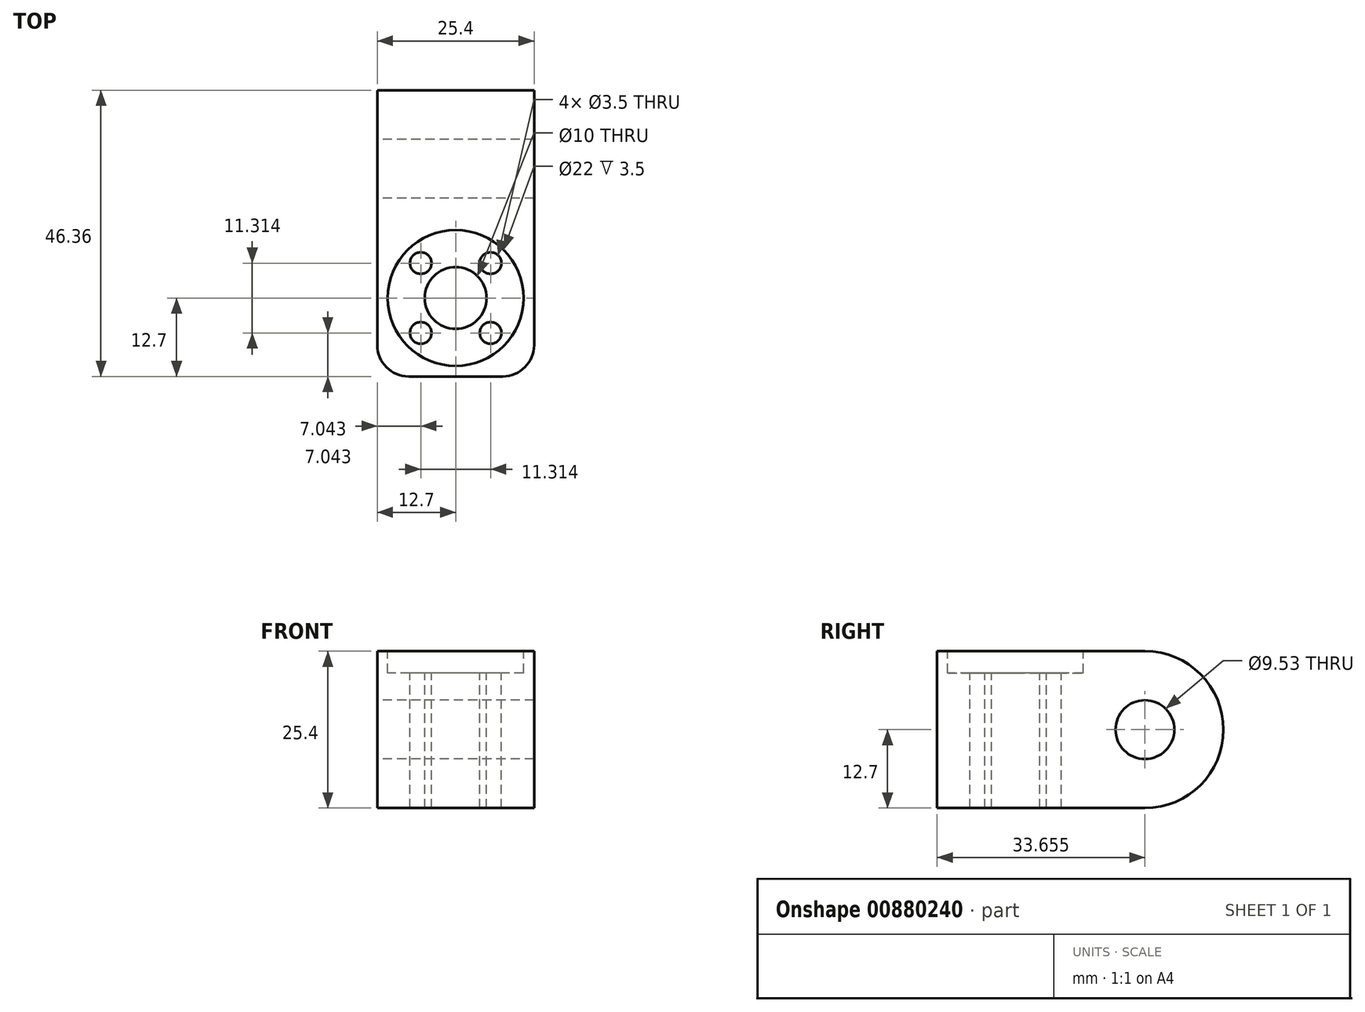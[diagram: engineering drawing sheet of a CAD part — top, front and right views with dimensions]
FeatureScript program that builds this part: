
annotation { "Feature Type Name" : "Feature", "Feature Type Description" : "" }
export const myFeature = defineFeature(function(context is Context, id is Id, definition is map)
    precondition{}
    {
        {
            var Q0;
            Q0=qCreatedBy(makeId("Top.planeOp"),FACE);
            var sketch = newSketch(context, id + "F0", { "sketchPlane" : qUnion([Q0])});
            skLineSegment(sketch, "E0.bottom", {"start": v(12.7, 12.7) * mm, "end": v(-12.7, 12.7) * mm});
            skLineSegment(sketch, "E0.top", {"start": v(12.7, -12.7) * mm, "end": v(-12.7, -12.7) * mm});
            skLineSegment(sketch, "E0.left", {"start": v(12.7, 12.7) * mm, "end": v(12.7, -12.7) * mm});
            skLineSegment(sketch, "E0.right", {"start": v(-12.7, 12.7) * mm, "end": v(-12.7, -12.7) * mm});
            skPoint(sketch, "E0.middle", {"position": v(0, 0) * mm});
            skSolve(sketch);
        }
        {
            var Q0;
            Q0=qSketchRegion(id+"F0",true);
            extrude(context, id + "F1", {"entities" : qUnion([Q0]), "depth" : 25.4 * mm});
        }
        {
            var Q0;
            Q0=qCreatedBy(makeId("Right.planeOp"),FACE);
            var sketch = newSketch(context, id + "F2", { "sketchPlane" : qUnion([Q0])});
            skCircle(sketch, "E1", {"center": v(20.96, 12.7) * mm, "radius": 4.76 * mm});
            skArc(sketch, "E2", {"start": v(20.96, 0) * mm, "mid": v(33.66, 12.7) * mm, "end": v(20.96, 25.4) * mm});
            skLineSegment(sketch, "E3", {"start": v(12.7, 25.4) * mm, "end": v(12.7, 0) * mm});
            skLineSegment(sketch, "E4", {"start": v(12.7, 0) * mm, "end": v(20.96, 0) * mm});
            skLineSegment(sketch, "E5", {"start": v(12.7, 25.4) * mm, "end": v(20.96, 25.4) * mm});
            skLineSegment(sketch, "E6", {"start": v(12.7, 12.7) * mm, "end": v(20.96, 12.7) * mm, "construction": true});
            skSolve(sketch);
        }
        {
            var Q0;
            Q0=qSketchRegion(id+"F2",true);
            var Q1;
            Q1=makeQuery(id+"F1.opExtrude","SWEPT_FACE",FACE,{"disambiguationData":[OSD([sQuery(id+"F0.wireOp",EDGE,"E0.left")])]});
            var Q2;
            Q2=makeQuery(id+"F1.opExtrude","SWEPT_FACE",FACE,{"disambiguationData":[OSD([sQuery(id+"F0.wireOp",EDGE,"E0.right")])]});
            extrude(context, id + "F3", {"entities" : qUnion([Q0]), "operationType" : NewBodyOperationType.ADD, "endBound" : BoundingType.UP_TO_SURFACE, "endBoundEntityFace" : qUnion([Q1]), "depth" : 11.43 * mm, "hasSecondDirection" : true, "secondDirectionBound" : BoundingType.UP_TO_SURFACE, "secondDirectionOppositeDirection" : true, "secondDirectionBoundEntityFace" : qUnion([Q2]), "secondDirectionDepth" : 6.35 * mm});
        }
        {
            var Q0;
            Q0=makeQuery(id+"FQh9y1oBI0PSwnX_1.boolean.opBoolean","MERGE",EDGE,{"derivedFrom":[makeQuery(id+"F1.opExtrude","SWEPT_EDGE",EDGE,{"disambiguationData":[OSD([sQuery(id+"F0.wireOp",EDGE,"E0.top"),sQuery(id+"F0.wireOp",EDGE,"E0.right")])]}),makeQuery(id+"FQh9y1oBI0PSwnX_1.opExtrude","SWEPT_EDGE",EDGE,{"disambiguationData":[OSD([sQuery(id+"FoaR56RkUjx8Qlo_1.wireOp",EDGE,"80af4be5-76a2-4d3a-8f25-b1f0519251b4.0"),sQuery(id+"FoaR56RkUjx8Qlo_1.wireOp",EDGE,"cc0fe09c-0044-47d0-847c-5cf717c9cb56.0")])]})]});
            var Q1;
            Q1=makeQuery(id+"FQh9y1oBI0PSwnX_1.boolean.opBoolean","MERGE",EDGE,{"derivedFrom":[makeQuery(id+"F1.opExtrude","SWEPT_EDGE",EDGE,{"disambiguationData":[OSD([sQuery(id+"F0.wireOp",EDGE,"E0.top"),sQuery(id+"F0.wireOp",EDGE,"E0.left")])]}),makeQuery(id+"FQh9y1oBI0PSwnX_1.opExtrude","SWEPT_EDGE",EDGE,{"disambiguationData":[OSD([sQuery(id+"FoaR56RkUjx8Qlo_1.wireOp",EDGE,"9dc4b1c0-afcf-448b-8161-34d6e761d681.0"),sQuery(id+"FoaR56RkUjx8Qlo_1.wireOp",EDGE,"80af4be5-76a2-4d3a-8f25-b1f0519251b4.0")])]})]});
            fillet(context, id + "F4", {"entities" : qUnion([Q0, Q1]), "radius" : 5.08 * mm, "tangentPropagation" : true, "allowEdgeOverflow" : false});
        }
        {
            var Q0;
            Q0=makeQuery(id+"F3.boolean.opBoolean","MERGE",FACE,{"derivedFrom":[makeQuery(id+"F1.opExtrude","CAP_FACE",FACE,{"disambiguationData":[OSD([sQuery(id+"F0.wireOp",EDGE,"E0.bottom"),sQuery(id+"F0.wireOp",EDGE,"E0.top"),sQuery(id+"F0.wireOp",EDGE,"E0.left"),sQuery(id+"F0.wireOp",EDGE,"E0.right")])],"isStart":false}),makeQuery(id+"F3.opExtrude","SWEPT_FACE",FACE,{"disambiguationData":[OSD([sQuery(id+"F2.wireOp",EDGE,"E5")])]})]});
            var sketch = newSketch(context, id + "F5", { "sketchPlane" : qUnion([Q0])});
            skCircle(sketch, "E7", {"center": v(0, 0) * mm, "radius": 5 * mm});
            skCircle(sketch, "E8", {"center": v(-5.66, 5.66) * mm, "radius": 1.75 * mm});
            skCircle(sketch, "E9", {"center": v(0, 0) * mm, "radius": 8 * mm, "construction": true});
            skCircle(sketch, "E10", {"center": v(5.66, 5.66) * mm, "radius": 1.75 * mm});
            skCircle(sketch, "E11", {"center": v(5.66, -5.66) * mm, "radius": 1.75 * mm});
            skCircle(sketch, "E12", {"center": v(-5.66, -5.66) * mm, "radius": 1.75 * mm});
            skLineSegment(sketch, "E13", {"start": v(5.66, 5.66) * mm, "end": v(-5.66, 5.66) * mm, "construction": true});
            skLineSegment(sketch, "E14", {"start": v(-5.66, -5.66) * mm, "end": v(-5.66, 5.66) * mm, "construction": true});
            skLineSegment(sketch, "E15", {"start": v(-5.66, -5.66) * mm, "end": v(5.66, -5.66) * mm});
            skSolve(sketch);
        }
        {
            var Q0;
            Q0=qSketchRegion(id+"F5",true);
            extrude(context, id + "F6", {"entities" : qUnion([Q0]), "operationType" : NewBodyOperationType.REMOVE, "endBound" : BoundingType.THROUGH_ALL, "oppositeDirection" : true, "depth" : 25.4 * mm});
        }
        {
            var Q0;
            Q0=makeQuery(id+"F3.boolean.opBoolean","MERGE",FACE,{"derivedFrom":[makeQuery(id+"F1.opExtrude","CAP_FACE",FACE,{"disambiguationData":[OSD([sQuery(id+"F0.wireOp",EDGE,"E0.bottom"),sQuery(id+"F0.wireOp",EDGE,"E0.top"),sQuery(id+"F0.wireOp",EDGE,"E0.left"),sQuery(id+"F0.wireOp",EDGE,"E0.right")])],"isStart":false}),makeQuery(id+"F3.opExtrude","SWEPT_FACE",FACE,{"disambiguationData":[OSD([sQuery(id+"F2.wireOp",EDGE,"E5")])]})]});
            var sketch = newSketch(context, id + "F7", { "sketchPlane" : qUnion([Q0])});
            skCircle(sketch, "E16", {"center": v(0, 0) * mm, "radius": 11 * mm});
            skSolve(sketch);
        }
        {
            var Q0;
            Q0=qSketchRegion(id+"F7",true);
            extrude(context, id + "F8", {"entities" : qUnion([Q0]), "operationType" : NewBodyOperationType.REMOVE, "oppositeDirection" : true, "depth" : 3.5 * mm});
        }
    });
